# Revit family: NBS_AndersonGECLtd_Snks_SeriesA_Double
name_source: partatom
category: Plumbing Fixtures
revit_build: Autodesk Revit 2017 (Build: 20160225_1515(x64)
units: mm (PartAtom-declared; Revit-internal decimal feet)

## family parameters
Cut with Voids When Loaded = No
Host = Face
Part Type = Normal
Room Calculation Point = No
Round Connector Dimension = Use Diameter
Shared = No

## types (9) — shared parameters
AssetType = Fixed
BowlDepth = 400 mm  [stored 1.31234 ft]
CW Connection = No
Category = Pr_40_20_96_81:Sinks
CodePerformance = EN 1.4301
CornerRadius = 15 mm  [stored 0.0492126 ft]
Description = Double bowled stainless steel sink
DrainDiameter = 89 mm  [stored 0.291995 ft]
DrainSize = 89 mm  [stored 0.291995 ft]
DurationUnit = year
ExpectedLife = 30 years
Features = Can be integrated with stainless steel worktops, basket strainer waste and , overflow fittings included
Finish = Bright satin
FlatFlange = 20 mm with corner radius of 10 mm
Form = Double bowled sink
HW Connection = No
IfcExportAs = IfcSanitaryTerminalType
IfcExportType = SINK
ManufacturerName = Anderson, GEC Ltd
ManufacturerURL = www.gecanderson.co.uk
Material = Stainless steel
Mounting = Inset, undermount, flushmount
NBSCertification = www.nationalbimlibrary.com/cert/yxecqxwy
NBSDescription = Sinks
NBSReference = 45-35-70/344
NominalHeight = 200 mm  [stored 0.656168 ft]
NominalLength = 440 mm  [stored 1.44357 ft]
Partition = 25 mm
ProductInformation = http://www.gecanderson.co.uk
Shape = Rectangle
SinkMaterial = NBS_Concept
SinkType = Other
SustainabilityPerformance = 100% Recyclable
Uniclass2015Code = Pr_40_20_96_81
Uniclass2015Title = Sinks
Uniclass2015Version = Products v1.11
Vent Connection = No
Version = 1
WarrantyDurationUnit = year
Waste Connection = Yes
zero-valued in all types: Default Elevation, WFU

## per-type parameters (varying)
| type | BIMObjectName | BowlHeightLeft | BowlHeightRight | BowlWidthLeft | BowlWidthRight | Name | NominalWidth | Size |
| AD34 | NBS_AndersonGECLtd_Sinks_AD34 | 200 mm  [stored 0.656168 ft] | 200 mm  [stored 0.656168 ft] | 340 mm  [stored 1.11549 ft] | 340 mm  [stored 1.11549 ft] | Sinks_AD34_AndersonGECLtd | 745 mm  [stored 2.44423 ft] | 745 x 440 x 200 mm |
| A3418 | NBS_AndersonGECLtd_Sinks_A3418 | 200 mm  [stored 0.656168 ft] | 170 mm | 340 mm  [stored 1.11549 ft] | 180 mm | Sinks_A3418_AndersonGECLtd | 585 mm | 585 x 440 x 200 mm |
| A1834 | NBS_AndersonGECLtd_Sinks_A1834 | 170 mm | 200 mm  [stored 0.656168 ft] | 180 mm | 340 mm  [stored 1.11549 ft] | Sinks_A1834_AndersonGECLtd | 585 mm | 585 x 440 x 200 mm |
| A5018 | NBS_AndersonGECLtd_Sinks_A5018 | 200 mm  [stored 0.656168 ft] | 170 mm | 500 mm | 180 mm | Sinks_A5018_AndersonGECLtd | 745 mm  [stored 2.44423 ft] | 745 x 440 x 200 mm |
| A1850 | NBS_AndersonGECLtd_Sinks_A1850 | 170 mm | 200 mm  [stored 0.656168 ft] | 180 mm | 500 mm | Sinks_A1850_AndersonGECLtd | 745 mm  [stored 2.44423 ft] | 745 x 440 x 200 mm |
| A5023 | NBS_AndersonGECLtd_Sinks_A5023 | 200 mm  [stored 0.656168 ft] | 170 mm | 500 mm | 230 mm | Sinks_A5023_AndersonGECLtd | 795 mm | 795 x 440 x 200 mm |
| A2350 | NBS_AndersonGECLtd_Sinks_A2350 | 170 mm | 200 mm  [stored 0.656168 ft] | 230 mm | 500 mm | Sinks_A2350_AndersonGECLtd | 795 mm | 795 x 440 x 200 mm |
| A5523 | NBS_AndersonGECLtd_Sinks_A5523 | 200 mm  [stored 0.656168 ft] | 170 mm | 550 mm | 230 mm | Sinks_A5523_AndersonGECLtd | 845 mm | 845 x 440 x 200 mm |
| A2355 | NBS_AndersonGECLtd_Sinks_A2355 | 170 mm | 200 mm  [stored 0.656168 ft] | 230 mm | 550 mm | Sinks_A2355_AndersonGECLtd | 845 mm | 845 x 440 x 200 mm |

note: column(s) folded — value = type name in every type: ModelNumber, ModelReference

note: [stored X ft] marks values corroborated as IEEE doubles in the binary element streams (Revit-internal decimal feet)

## geometry (parser evidence)
native form markers: Sweep x2
no freeform markers — native parametric forms only
